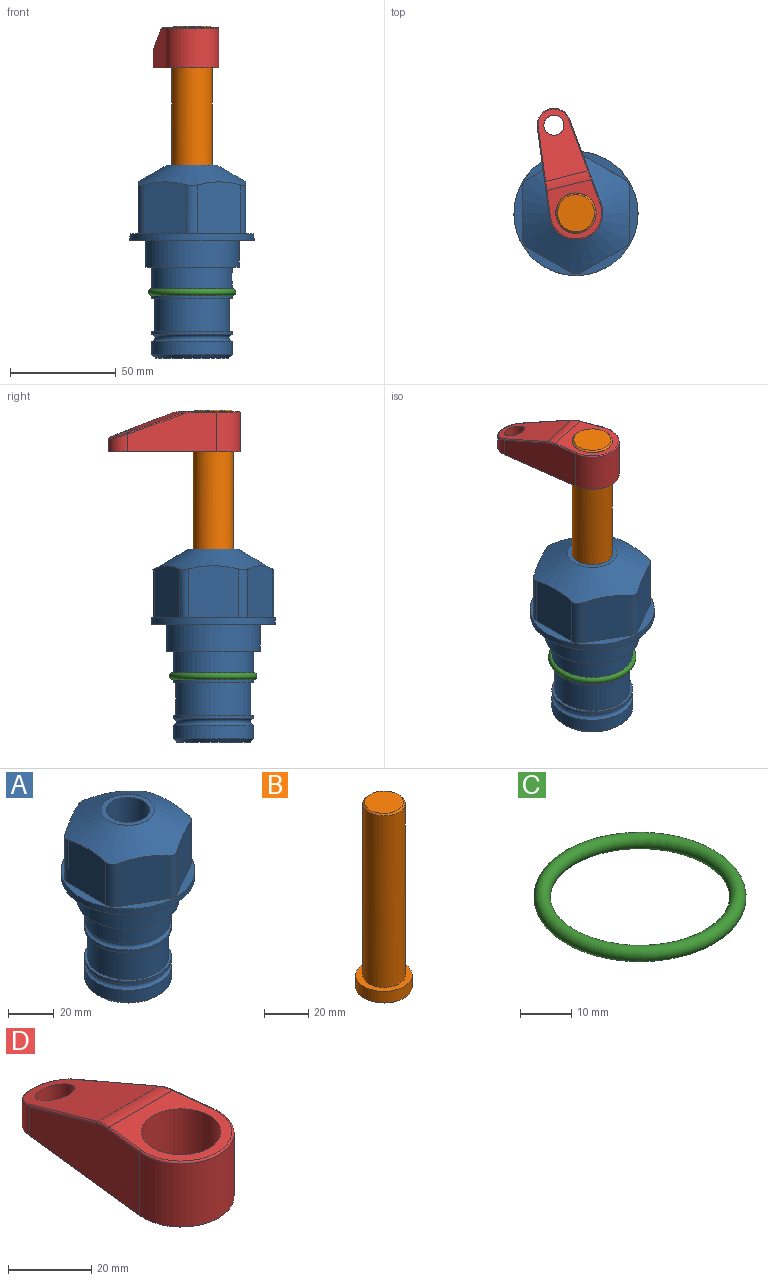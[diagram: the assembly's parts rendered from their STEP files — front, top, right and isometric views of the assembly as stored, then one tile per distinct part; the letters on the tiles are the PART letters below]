
ASSEMBLY  parts=4 mates=2
PART A: 36 faces, bbox 58.7x58.7x91.2 mm
  f0: cylinder r=17.78mm len=35.56mm, axis (0,0,1), area 1670.8mm2, adj f23,f24,f31
  f1: cylinder r=19.05mm len=38.1mm, axis (0,0,1), area 1191.9mm2, adj f26,f27,f30
  f2: plane 58.66x58.66mm, normal (0,0,-1), area 1150.6mm2, adj f3,f28
  f3: cylinder r=29.33mm len=58.66mm, axis (0,0,-1), area 585.1mm2, adj f2,f4
  f4: plane 58.66x58.66mm, normal (0,0,1), area 475.9mm2, adj f3,f5,f6,f7,f8,f9,f10,f11
  f5: plane 24.5x20.32mm, normal (-0.5,0.87,0), area 562.8mm2, adj f4,f15,f16,f17
  f6: plane 24.5x20.32mm, normal (0.5,0.87,0), area 562.8mm2, adj f4,f14,f15,f17
  f7: plane 24.5x23.48mm, normal (1,0,0), area 562.8mm2, adj f4,f13,f14,f17
  f8: plane 24.5x20.32mm, normal (0.5,-0.87,0), area 562.8mm2, adj f4,f12,f13,f17
  f9: plane 24.5x20.32mm, normal (-0.5,-0.87,0), area 562.8mm2, adj f4,f11,f12,f17
  f10: plane 24.5x23.48mm, normal (-1,0,0), area 562.8mm2, adj f4,f11,f16,f17
  f11: cylinder r=5.08mm len=23.01mm, axis (0,0,-1), area 121.2mm2, adj f4,f9,f10,f17
  f12: cylinder r=5.08mm len=23.01mm, axis (0,0,-1), area 121.2mm2, adj f4,f8,f9,f17
  f13: cylinder r=5.08mm len=23.01mm, axis (0,0,-1), area 121.2mm2, adj f4,f7,f8,f17
  f14: cylinder r=5.08mm len=23.01mm, axis (0,0,-1), area 121.2mm2, adj f4,f6,f7,f17
  f15: cylinder r=5.08mm len=23.01mm, axis (0,0,-1), area 121.2mm2, adj f4,f5,f6,f17
  f16: cylinder r=5.08mm len=23.01mm, axis (0,0,-1), area 121.2mm2, adj f4,f5,f10,f17
  f17: cone r=11.73mm half-angle=60deg, axis (0,0,-1), area 2071.8mm2, adj f5,f6,f7,f8,f9,f10,f11,f12
  f18: plane 23.46x23.46mm, normal (0,0,1), area 147.4mm2, adj f17,f35
  f19: plane 34.93x34.93mm, normal (0,0,-1), area 958mm2, adj f29
  f20: cylinder r=19.05mm len=38.1mm, axis (0,0,1), area 760.1mm2, adj f21,f29
  f21: torus R=19.05mm, axis (0,0,1), area 565.3mm2, adj f20,f22
  f22: cylinder r=19.05mm len=38.1mm, axis (0,0,1), area 190mm2, adj f21,f23
  f23: plane 38.1x38.1mm, normal (0,0,1), area 146.9mm2, adj f0,f22
  f24: plane 38.1x38.1mm, normal (0,0,-1), area 146.9mm2, adj f0,f25
  f25: cylinder r=19.05mm len=38.1mm, axis (0,0,1), area 190mm2, adj f24,f26
  f26: torus R=19.05mm, axis (0,0,1), area 565.3mm2, adj f1,f25
  f27: plane 44.45x44.45mm, normal (0,0,-1), area 411.7mm2, adj f1,f28
  f28: cylinder r=22.23mm len=44.45mm, axis (0,0,1), area 1773.5mm2, adj f2,f27
  f29: cone r=19.05mm half-angle=45deg, axis (0,0,1), area 257.5mm2, adj f19,f20
  f30: cylinder r=3.17mm len=6.75mm, axis (-1,0,0), area 128mm2, adj f1,f33
  f31: cylinder r=3.17mm len=6.35mm, axis (-1,0,0), area 102.5mm2, adj f0,f33
  f32: plane 25.4x25.4mm, normal (0,0,1), area 506.7mm2, adj f33
  f33: cylinder r=12.7mm len=66.42mm, axis (0,0,-1), area 5236.2mm2, adj f30,f31,f32,f34
  f34: cone r=9.53mm half-angle=30deg, axis (0,0,-1), area 443.4mm2, adj f33,f35
  f35: cylinder r=9.53mm len=19.05mm, axis (0,0,-1), area 849mm2, adj f18,f34
PART B: 6 faces, bbox 25.4x25.4x101.6 mm
  f0: plane 17.46x17.46mm, normal (0,0,1), area 239.5mm2, adj f5
  f1: plane 25.4x25.4mm, normal (0,0,-1), area 506.7mm2, adj f2
  f2: cylinder r=12.7mm len=25.4mm, axis (0,0,1), area 506.7mm2, adj f1,f3
  f3: plane 25.4x25.4mm, normal (0,0,1), area 221.7mm2, adj f2,f4
  f4: cylinder r=9.53mm len=94.46mm, axis (0,0,1), area 5653mm2, adj f3,f5
  f5: cone r=8.73mm half-angle=45deg, axis (0,0,-1), area 64.4mm2, adj f0,f4
PART C: 1 faces, bbox 44.7x44.7x3.2 mm
  f0: torus R=19.05mm, axis (0,0,1), area 1193.9mm2
PART D: 44 faces, bbox 27.5x64.5x19.1 mm
  f0: plane 2.3x0.95mm, normal (0,0,-1), area 1mm2, adj f25,f30,f34
  f1: plane 63.5x25.4mm, normal (0,0,-1), area 561.7mm2, adj f2,f3,f4,f5,f6,f7,f19,f20
  f2: cylinder r=12.7mm len=25.4mm, axis (0,0,-1), area 792.2mm2, adj f1,f3,f5,f13
  f3: plane 42.33x18.54mm, normal (0.99,0.11,0), area 647mm2, adj f1,f2,f4,f11,f12,f14
  f4: cylinder r=7.94mm len=15.78mm, axis (0,0,-1), area 158.6mm2, adj f1,f3,f5,f16
  f5: plane 42.33x18.54mm, normal (-0.99,0.11,0), area 647mm2, adj f1,f2,f4,f15,f17,f18
  f6: cylinder r=9.53mm len=19.05mm, axis (0,0,-1), area 1140.1mm2, adj f1,f8
  f7: cylinder r=4.76mm len=10.98mm, axis (0,0,-1), area 276.1mm2, adj f1,f9
  f8: plane 25.83x24.38mm, normal (0,0,1), area 262.2mm2, adj f6,f10,f11,f13,f15
  f9: plane 32.49x20.55mm, normal (0,0.34,0.94), area 489.9mm2, adj f7,f10,f14,f16,f18
  f10: cylinder r=12.7mm len=21.49mm, axis (-1,0,0), area 93.2mm2, adj f8,f9,f12,f17
  f11: cylinder r=0.51mm len=12.34mm, axis (0.11,-0.99,0), area 9.9mm2, adj f3,f8,f12,f13
  f12: bspline ~7.62x1.64mm, area 3.5mm2, adj f3,f10,f11,f14
  f13: torus R=12.19mm, axis (0,0,1), area 33.6mm2, adj f2,f8,f11,f15
  f14: cylinder r=0.51mm len=26.01mm, axis (0.1,-0.93,0.34), area 21.6mm2, adj f3,f9,f12,f16
  f15: cylinder r=0.51mm len=12.34mm, axis (0.11,0.99,0), area 9.9mm2, adj f5,f8,f13,f17
  f16: bspline ~15.78x7.05mm, area 15.7mm2, adj f4,f9,f14,f18
  f17: bspline ~7.62x1.64mm, area 3.5mm2, adj f5,f10,f15,f18
  f18: cylinder r=0.51mm len=26.01mm, axis (0.1,0.93,-0.34), area 21.6mm2, adj f5,f9,f16,f17
  f19: plane 21.6x14.29mm, normal (-0.99,-0.11,0), area 242.6mm2, adj f1,f26,f28,f34,f36,f38
  f20: plane 21.6x14.29mm, normal (0.99,-0.11,0), area 242.6mm2, adj f1,f27,f29,f37,f39,f41
  f21: cylinder r=12.7mm len=14.29mm, axis (0,0,-1), area 173.2mm2, adj f1,f26,f27,f30,f31,f33
  f22: cylinder r=7.94mm len=7.63mm, axis (0,0,-1), area 53.8mm2, adj f1,f28,f29,f42
  f23: plane 2.3x0.95mm, normal (0,0,-1), area 1mm2, adj f25,f33,f37
  f24: plane 17.94x12.32mm, normal (0,-0.34,-0.94), area 191.2mm2, adj f25,f38,f41,f42
  f25: cylinder r=9.53mm len=12.93mm, axis (-1,0,0), area 37.5mm2, adj f0,f23,f24,f31,f36,f39
  f26: cylinder r=1.59mm len=14.29mm, axis (0,0,-1), area 49mm2, adj f1,f19,f21,f32
  f27: cylinder r=1.59mm len=14.29mm, axis (0,0,-1), area 49mm2, adj f1,f20,f21,f35
  f28: cylinder r=1.59mm len=7.28mm, axis (0,0,-1), area 22.1mm2, adj f1,f19,f22,f40
  f29: cylinder r=1.59mm len=7.28mm, axis (0,0,-1), area 22.1mm2, adj f1,f20,f22,f43
  f30: torus R=14.29mm, axis (0,0,1), area 5.8mm2, adj f0,f21,f31,f32
  f31: bspline ~11.06x2.73mm, area 20.8mm2, adj f21,f25,f30,f33
  f32: sphere r=1.59mm, area 5.4mm2, adj f26,f30,f34
  f33: torus R=14.29mm, axis (0,0,1), area 5.8mm2, adj f21,f23,f31,f35
  f34: cylinder r=1.59mm len=1.68mm, axis (-0.11,0.99,0), area 2.4mm2, adj f0,f19,f32,f36
  f35: sphere r=1.59mm, area 5.4mm2, adj f27,f33,f37
  f36: bspline ~5.82x2.33mm, area 7.7mm2, adj f19,f25,f34,f38
  f37: cylinder r=1.59mm len=1.68mm, axis (0.11,0.99,0), area 2.4mm2, adj f20,f23,f35,f39
  f38: cylinder r=1.59mm len=18.33mm, axis (0.1,-0.93,0.34), area 46.7mm2, adj f19,f24,f36,f40
  f39: bspline ~5.82x2.33mm, area 7.7mm2, adj f20,f25,f37,f41
  f40: sphere r=1.59mm, area 3.6mm2, adj f28,f38,f42
  f41: cylinder r=1.59mm len=18.33mm, axis (0.1,0.93,-0.34), area 46.7mm2, adj f20,f24,f39,f43
  f42: bspline ~8.31x1.84mm, area 15.3mm2, adj f22,f24,f40,f43
  f43: sphere r=1.59mm, area 3.6mm2, adj f29,f41,f42
PLACE A at identity fixed
PLACE B rot(axis=(0,0,1),14.1deg) t=(0,0,27.63)mm
PLACE C at identity
PLACE D rot(axis=(0,0,1),14.1deg) t=(0,0,81.44)mm
MATE cylindrical B.f2 <-> A.f0  axis (0,0,1) through (0,0,53.27)mm
MATE fastened B.f2 <-> D.f2  axis (0,0,-1) through (0,0,100.49)mm
